# Revit family: Приточная вентустановка Naveka Node4
name_source: partatom
category: Оборудование
units: mm (PartAtom-declared; Revit-internal decimal feet)

## family parameters
Всегда вертикально = Да
Заголовок OmniClass = Climate Control (HVAC)
На основе рабочей плоскости = Нет
Номер OmniClass = 23.75.00.00
Общий = Нет
При загрузке вырезать с полостями = Нет
Размер круглого соединителя = Использовать диаметр
Тип детали = Нормальный
Точка расчета площади = Нет

## types (14) — shared parameters
ADSK_Единица измерения = шт.
ADSK_Завод-изготовитель = Naveka
ADSK_Наименование = Установка вентиляционная Node4
ADSK_Примечание = https://progress-nw.ru
Материал = RAL 0000 Серый металл

## per-type parameters (varying)
| type | ADSK_Марка | ADSK_Масса | B | D | D+0.5 | D+4.5 | H | L | b | d | Мощность вентиляторов, кВт | Мощность калорифера, кВт | Питание, В | Сила вентилятора, А | Ток ТЭНа (на фазу), А |
| Node4-100/E1 | Node4-100/E1 | 25 | 450 мм | 49 мм | 50 мм | 54 мм | 250 мм | 930 мм | 125 мм | 100 мм | 0.06 | 1 | 1-220 | 0.3 | 4.5 |
| Node4-125/E1.5 | Node4-100/E1.5 | 30 | 490 мм | 62 мм | 62 мм | 66 мм | 250 мм | 935 мм | 125 мм | 125 мм | 0.06 | 1.5 | 1-220 | 0.3 | 6.8 |
| Node4-160/E2 | Node4-160/E2 | 33 | 520 мм | 79 мм | 80 мм | 84 мм | 294 мм | 965 мм | 150 мм | 160 мм | 0.09 | 2 | 1-220 | 0.4 | 9.1 |
| Node4-200/E4.5 | Node4-200/E4.5 | 41 | 550 мм | 99 мм | 100 мм | 104 мм | 370 мм | 965 мм | 176 мм | 200 мм | 0.14 | 4.5 | 3-380 | 0.6 | 13.6 |
| Node4-250/E7.5 | Node4-250/E7.5 | 43 | 600 мм | 124 мм | 125 мм | 129 мм | 390 мм | 965 мм | 185 мм | 250 мм | 0.21 | 7.5 | 3-380 | 1 | 9.1 |
| Node4-315/E9 | Node4-315/E9 | 50 | 600 мм | 157 мм | 157 мм | 161 мм | 438 мм | 1044 мм | 217 мм | 315 мм | 0.23 | 9 | 3-380 | 1 | 13.6 |
| Node4-125/E2 | Node4-100/E2 | 30 | 490 мм | 62 мм | 62 мм | 66 мм | 250 мм | 935 мм | 125 мм | 125 мм | 0.06 | 2 | 1-220 | 0.3 | 9.1 |
| Node4-160/E4.5 | Node4-160/E4.5 | 33 | 520 мм | 79 мм | 80 мм | 84 мм | 294 мм | 965 мм | 150 мм | 160 мм | 0.09 | 4.5 | 1-220 | 0.4 | 13.6 |
| Node4-200/E6 | Node4-200/E6 | 41 | 550 мм | 99 мм | 100 мм | 104 мм | 370 мм | 965 мм | 176 мм | 200 мм | 0.14 | 6 | 3-380 | 0.6 | 9.1 |
| Node4-250/E9 | Node4-250/E9 | 43 | 600 мм | 124 мм | 125 мм | 129 мм | 390 мм | 965 мм | 185 мм | 250 мм | 0.21 | 9 | 3-380 | 1 | 13.6 |
| Node4-315/E12 | Node4-315/E12 | 50 | 600 мм | 157 мм | 157 мм | 161 мм | 438 мм | 1044 мм | 217 мм | 315 мм | 0.23 | 12 | 3-380 | 1 | 18.2 |
| Node4-315/E15 | Node4-315/E15 | 50 | 600 мм | 157 мм | 157 мм | 161 мм | 438 мм | 1044 мм | 217 мм | 315 мм | 0.23 | 15 | 3-380 | 1 | 22.7 |
| Node4-315/W2 | Node4-315/W2 | 50 | 600 мм | 157 мм | 157 мм | 161 мм | 438 мм | 1044 мм | 217 мм | 315 мм | 0.23 | - | 3-380 | 1 | - |
| Node4-315/W3 | Node4-315/W3 | 50 | 600 мм | 157 мм | 157 мм | 161 мм | 438 мм | 1044 мм | 217 мм | 315 мм | 0.23 | - | 3-380 | 1 | - |
